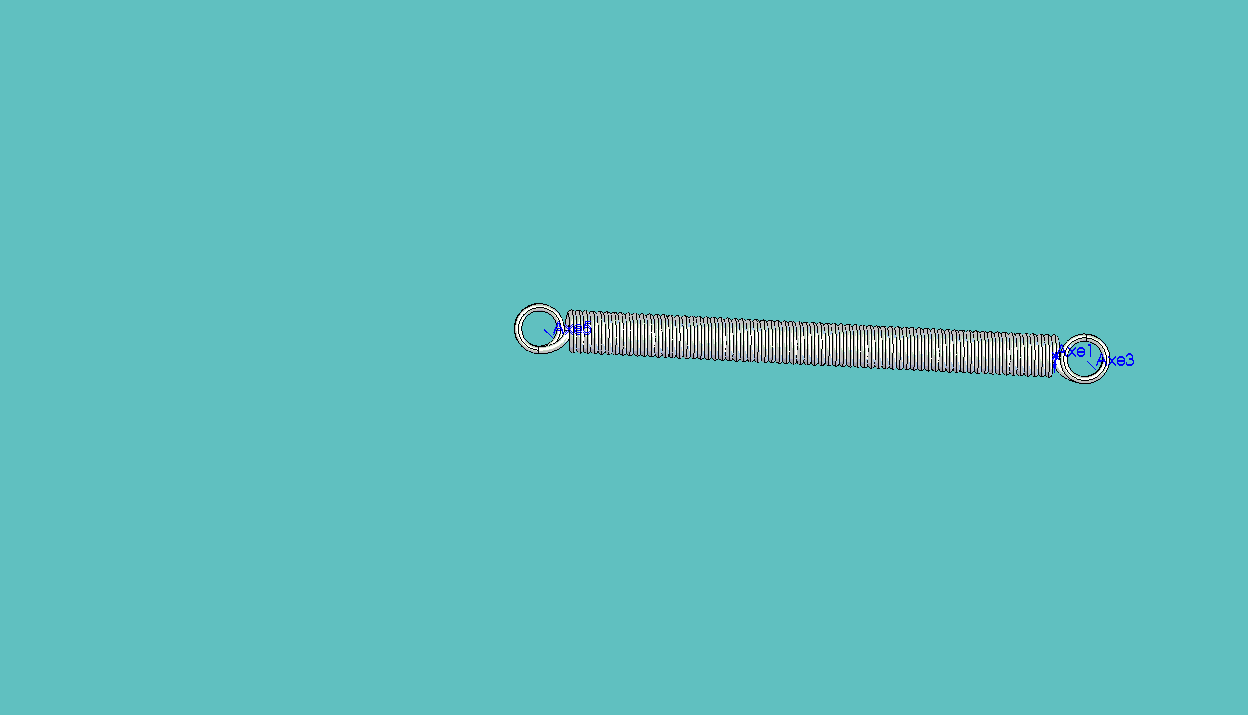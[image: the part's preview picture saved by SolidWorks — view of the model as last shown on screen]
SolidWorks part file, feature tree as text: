
SOLIDWORKS PART (.sldprt)
format: sldprt  version: not decoded by parser v0  size: 6,294,528 bytes
history: native  units: mm
features: sketch x7, plane x5, sweep x3, material x1, helix x1, pattern_circular x1 (+8 scaffold rows collapsed)
feature tree (26):
  scaffold x8  (default folders/planes/origin — collapsed)
  material  "Matériau <non spécifié>"
  plane  "Plan de face"
  plane  "Plan de dessus"
  plane  "Plan de droite"
  sketch  "Esquisse1"  dims[D1=4.5mm]
  helix  "Hélice/Spirale1"  Pitch=61.65mm
  sketch  "Esquisse2"  dims[D2=0.9mm D1=2.25mm]
  sweep  "Balayage1"
  sketch  "Esquisse3"  dims[D1=0.0mm]
  plane  "Plan1"
  sketch  "Esquisse5"  dims[D1=3.6mm D2=2.7mm]
  sweep  "Balayage2"
  sketch  "Esquisse6"
  sketch  "Esquisse9"  dims[D1=2.7mm Hélice/Spirale4=0.0 D3=1.35mm D4=0.9mm D5=1500.0mm D7=90.0deg]
  sweep  "Balayage5"
  plane  "Plan4"  Offset=30.825mm
  pattern_circular  "Répétition circulaire1"  Count=2 Angle=180deg
  sketch  "Esquisse12"  dims[D1=2.7mm]
decode coverage: 8 of 12 modeling features carry decoded parameters
note: suppression state not decoded; provenance and decode notes live in map.json
